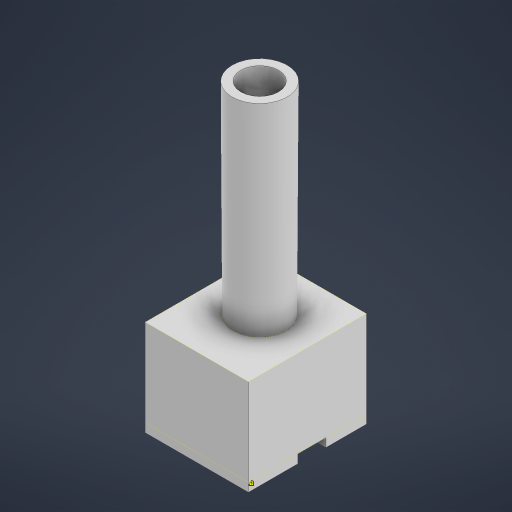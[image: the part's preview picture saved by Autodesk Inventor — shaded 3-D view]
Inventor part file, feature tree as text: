
AUTODESK INVENTOR PART (.ipt)
format: ipt  version: 2024.1 (Build 281209000, 209)  size: 1,758,720 bytes
history: native  units: mm
features: projected_geometry x23, sketch x18, extrude x12, loft x2, plane x1
ambient origin geometry x8: Origin, YZ Plane, XZ Plane, XY Plane, X Axis, Y Axis, Z Axis, Center Point
bodies: Solid1 (feature_tree)
feature tree (56):
  extrude  "Extrusion1"  Depth=3.0mm
  extrude  "Extrusion2"  TaperAngle=0.0deg  [1 undecoded]
  extrude  "Extrusion3"  Depth=10.0mm TaperAngle=0.0deg
  extrude  "Extrusion4"  Depth=0.5mm
  extrude  "Extrusion5"  Depth=0.5mm
  sketch  "Sketch6"  dims[d14=0.5mm d15=0.5mm]
  plane  "Work Plane1"
  extrude  "Extrusion16"  Depth=0.5mm
  loft  "Loft1"
  loft  "Loft2"
  extrude  "Extrusion6"  Depth=0.5mm
  extrude  "Extrusion8"  Depth=0.5mm
  extrude  "Extrusion9"  Depth=0.5mm
  extrude  "Extrusion10"  Depth=0.5mm
  extrude  "Extrusion11"  Depth=0.5mm
  extrude  "Extrusion12"  Depth=0.5mm
  sketch  "Sketch23"  dims[d34=0.5mm]
  sketch  "Sketch24"  dims[d35=0.5mm d36=0.5mm d37=0.5mm d38=10.0mm d39=0.0mm d40=12.0mm d41=100.0mm d42=13.0mm d43=3.0mm d44=3.0mm d45=0.0mm d46=90.0deg d47=0.0mm d48=90.0deg d49=13.0mm d50=0.0mm d51=90.0deg d52=0.0mm d53=90.0deg d55=7.0mm d56=17.0mm d57=14.0mm d58=0.0mm d59=0.0mm d64=25.0mm d65=0.0mm d66=25.0mm d67=0.0mm d68=25.0mm d69=0.0mm d70=3.0mm d71=1.0mm d72=1.0mm d73=10.0mm d74=0.0mm d75=10.0mm d76=0.0mm d84=30.0mm d85=0.0mm]
  sketch  "Sketch1"  dims[d0=3.0mm d1=0.0mm d2=0.2mm]
  sketch  "Sketch2"  dims[d3=1.0mm d4=0.0mm d5=0.0mm]
  sketch  "Sketch3"  dims[d6=10.0mm d7=0.0mm d8=10.0mm d9=0.0mm]
  sketch  "Sketch4"  dims[d10=0.5mm d11=0.5mm]
  sketch  "Sketch5"  dims[d12=0.5mm d13=0.5mm]
  sketch  "Sketch7"  dims[d16=0.5mm d17=0.5mm]
  sketch  "Sketch8"  dims[d18=0.5mm d19=0.5mm]
  sketch  "Sketch9"  dims[d20=0.5mm d21=0.5mm]
  sketch  "Sketch11"  dims[d22=0.5mm d23=0.5mm]
  sketch  "Sketch13"  dims[d24=0.5mm d25=0.5mm]
  projected_geometry  "Projected Loop2"
  projected_geometry  "Projected Loop3"
  projected_geometry  "Projected Loop4"
  projected_geometry  "Projected Loop5"
  projected_geometry  "Projected Loop6"
  projected_geometry  "Projected Loop7"
  projected_geometry  "Projected Loop8"
  projected_geometry  "Projected Loop9"
  projected_geometry  "Projected Loop10"
  projected_geometry  "Projected Loop11"
  projected_geometry  "Projected Loop12"
  projected_geometry  "Projected Loop13"
  projected_geometry  "Projected Loop14"
  projected_geometry  "Projected Loop15"
  projected_geometry  "Projected Loop16"
  projected_geometry  "Projected Loop17"
  sketch  "Sketch14"  dims[d26=0.5mm d27=0.5mm]
  sketch  "Sketch15"  dims[d28=0.5mm d29=0.5mm]
  projected_geometry  "Projected Loop18"
  sketch  "Sketch16"  dims[d30=0.5mm d31=0.5mm]
  sketch  "Sketch17"  dims[d32=0.5mm]
  projected_geometry  "Projected Loop19"
  sketch  "Sketch22"  dims[d33=0.5mm]
  projected_geometry  "Project Cut Edges1"
  projected_geometry  "Project Cut Edges2"
  projected_geometry  "Project Cut Edges3"
  projected_geometry  "Project Cut Edges6"
  projected_geometry  "Project Cut Edges7"
note: 1 required parameter value undecoded (feature->parameter linkage not recoverable at this tier; creation-order binding heuristic only, values carry confidence <= 0.55)
